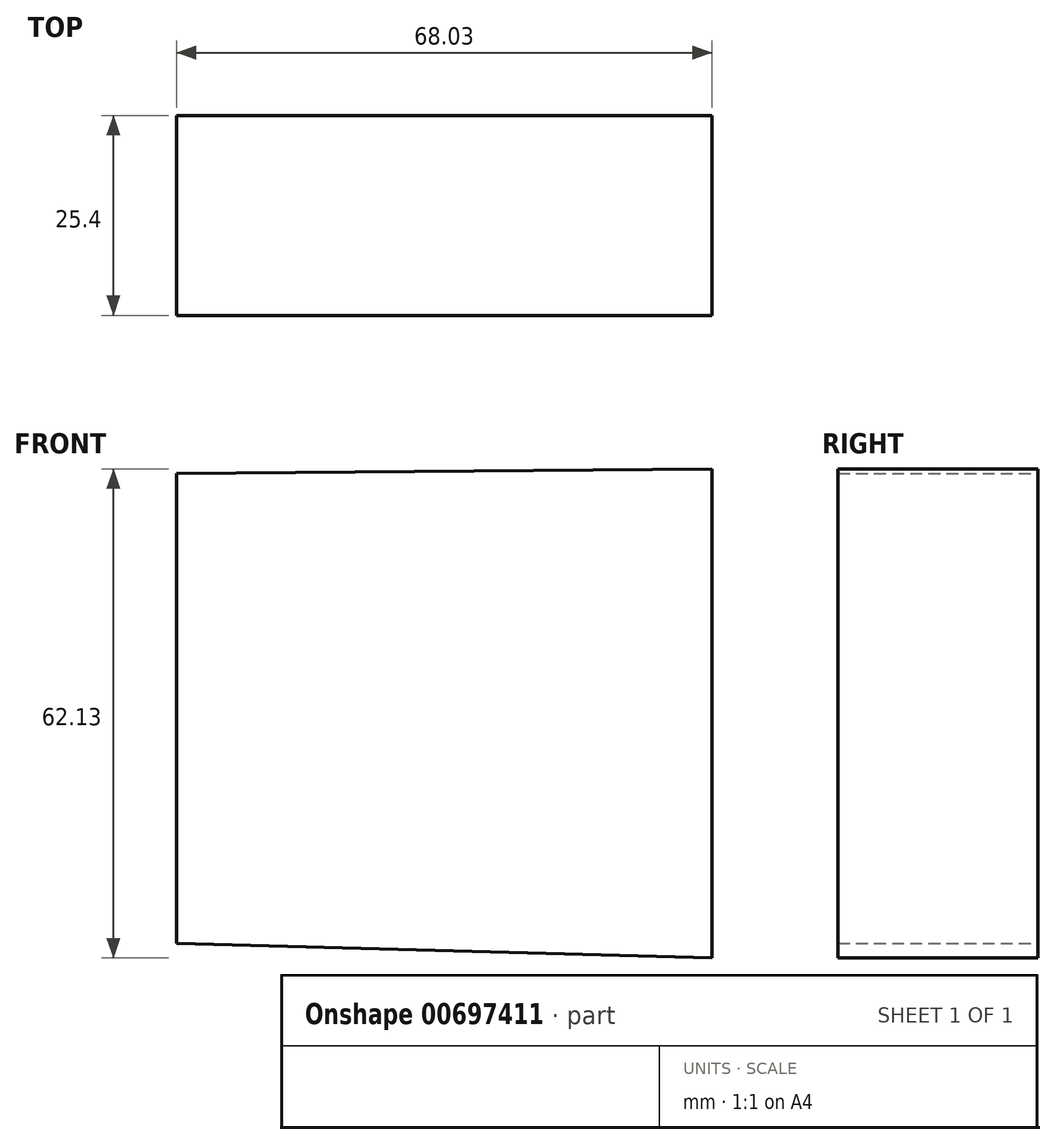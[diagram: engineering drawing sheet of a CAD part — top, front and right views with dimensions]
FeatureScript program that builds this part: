
annotation { "Feature Type Name" : "Feature", "Feature Type Description" : "" }
export const myFeature = defineFeature(function(context is Context, id is Id, definition is map)
    precondition{}
    {
        {
            var Q0;
            Q0=qCreatedBy(makeId("Front.planeOp"),FACE);
            var sketch = newSketch(context, id + "F0", { "sketchPlane" : qUnion([Q0])});
            skLineSegment(sketch, "E0", {"start": v(-30.7, 36.78) * mm, "end": v(-30.7, -22.95) * mm});
            skLineSegment(sketch, "E1", {"start": v(-30.7, -22.95) * mm, "end": v(37.33, -24.8) * mm});
            skLineSegment(sketch, "E2", {"start": v(37.33, -24.8) * mm, "end": v(37.33, 37.33) * mm});
            skLineSegment(sketch, "E3", {"start": v(37.33, 37.33) * mm, "end": v(-30.7, 36.78) * mm});
            skSolve(sketch);
        }
        {
            var Q0;
            Q0 = qSketchRegion(id + "F0", true);
            extrude(context, id + "F1", {"entities" : qUnion([Q0]), "depth" : 25.4 * mm, "offsetDistance" : 25.4 * mm});
        }
    });
